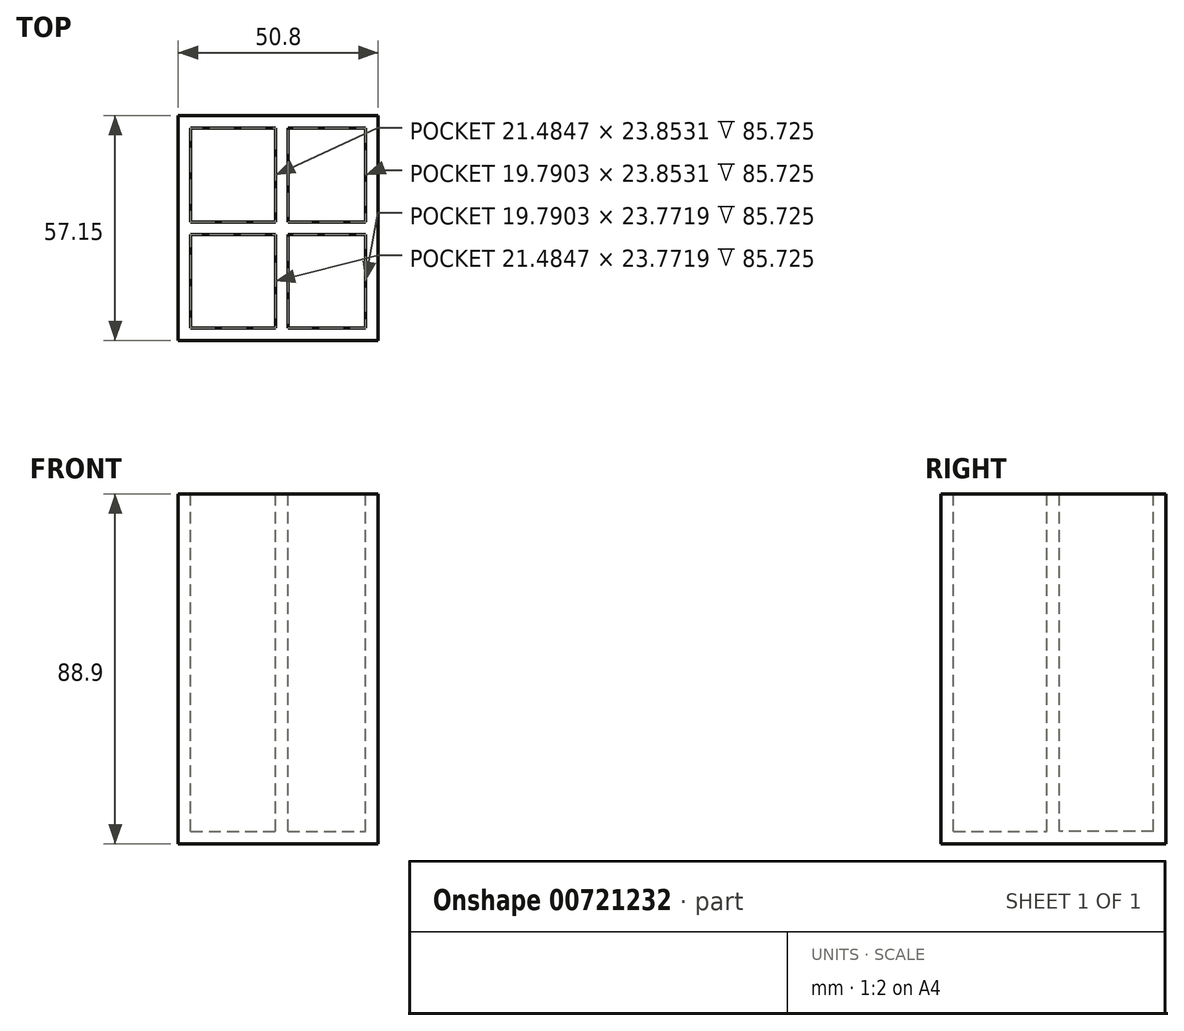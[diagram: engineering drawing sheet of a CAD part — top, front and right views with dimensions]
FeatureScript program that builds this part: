
annotation { "Feature Type Name" : "Feature", "Feature Type Description" : "" }
export const myFeature = defineFeature(function(context is Context, id is Id, definition is map)
    precondition{}
    {
        {
            var Q0;
            Q0=qCreatedBy(makeId("Top.planeOp"),FACE);
            var sketch = newSketch(context, id + "F0", { "sketchPlane" : qUnion([Q0])});
            skLineSegment(sketch, "E0.bottom", {"start": v(-26.25, 28.62) * mm, "end": v(24.55, 28.62) * mm});
            skLineSegment(sketch, "E0.top", {"start": v(-26.25, -28.53) * mm, "end": v(24.55, -28.53) * mm});
            skLineSegment(sketch, "E0.left", {"start": v(-26.25, 28.62) * mm, "end": v(-26.25, -28.53) * mm});
            skLineSegment(sketch, "E0.right", {"start": v(24.55, 28.62) * mm, "end": v(24.55, -28.53) * mm});
            skSolve(sketch);
        }
        {
            var Q0;
            Q0=makeQuery(id+"F0.imprint","IMPRINT",FACE,{"disambiguationData":[TD([[makeQuery(id+"F0.imprint","IMPRINT",EDGE,{"derivedFrom":sQuery(id+"F0.wireOp",EDGE,"E0.bottom")}),-1.0]])]});
            extrude(context, id + "F1", {"entities" : qUnion([Q0]), "depth" : 88.9 * mm, "offsetDistance" : 25.4 * mm});
        }
        {
            var Q0;
            Q0=makeQuery(id+"F1.opExtrude","CAP_FACE",FACE,{"disambiguationData":[OSD([sQuery(id+"F0.wireOp",EDGE,"E0.bottom"),sQuery(id+"F0.wireOp",EDGE,"E0.top"),sQuery(id+"F0.wireOp",EDGE,"E0.left"),sQuery(id+"F0.wireOp",EDGE,"E0.right")])],"isStart":false});
            var sketch = newSketch(context, id + "F2", { "sketchPlane" : qUnion([Q0])});
            skPoint(sketch, "E1.endSnap0", {"position": v(-0.85, -28.53) * mm});
            skLineSegment(sketch, "E2", {"start": v(-23.07, 1.59) * mm, "end": v(-1.59, 1.59) * mm});
            skLineSegment(sketch, "E3", {"start": v(-23.07, -1.59) * mm, "end": v(-1.59, -1.59) * mm});
            skLineSegment(sketch, "E4", {"start": v(-1.59, -25.36) * mm, "end": v(-1.59, -1.59) * mm});
            skLineSegment(sketch, "E5", {"start": v(1.59, -25.36) * mm, "end": v(1.59, -1.59) * mm});
            skLineSegment(sketch, "E6", {"start": v(-23.07, 25.44) * mm, "end": v(-23.07, 1.59) * mm});
            skLineSegment(sketch, "E7", {"start": v(-23.07, -25.36) * mm, "end": v(-1.59, -25.36) * mm});
            skLineSegment(sketch, "E8", {"start": v(21.38, 25.44) * mm, "end": v(21.38, 1.59) * mm});
            skLineSegment(sketch, "E9", {"start": v(-23.07, 25.44) * mm, "end": v(-1.59, 25.44) * mm});
            skLineSegment(sketch, "E10.trimOffspring", {"start": v(1.59, 1.59) * mm, "end": v(21.38, 1.59) * mm});
            skLineSegment(sketch, "E11.trimOffspring", {"start": v(1.59, 1.59) * mm, "end": v(1.59, 25.44) * mm});
            skLineSegment(sketch, "E12.trimOffspring", {"start": v(1.59, -1.59) * mm, "end": v(21.38, -1.59) * mm});
            skLineSegment(sketch, "E13.trimOffspring", {"start": v(-1.59, 1.59) * mm, "end": v(-1.59, 25.44) * mm});
            skLineSegment(sketch, "E14.trimOffspring", {"start": v(21.38, -1.59) * mm, "end": v(21.38, -25.36) * mm});
            skLineSegment(sketch, "E15.trimOffspring", {"start": v(1.59, -25.36) * mm, "end": v(21.38, -25.36) * mm});
            skLineSegment(sketch, "E16.trimOffspring", {"start": v(-23.07, -1.59) * mm, "end": v(-23.07, -25.36) * mm});
            skLineSegment(sketch, "E17.trimOffspring", {"start": v(1.59, 25.44) * mm, "end": v(21.38, 25.44) * mm});
            skSolve(sketch);
        }
        {
            var Q0;
            Q0=makeQuery(id+"F2.imprint","IMPRINT",FACE,{"disambiguationData":[TD([[makeQuery(id+"F2.imprint","IMPRINT",EDGE,{"derivedFrom":sQuery(id+"F2.wireOp",EDGE,"E2")}),1.0]])]});
            var Q1;
            Q1=makeQuery(id+"F2.imprint","IMPRINT",FACE,{"disambiguationData":[TD([[makeQuery(id+"F2.imprint","IMPRINT",EDGE,{"derivedFrom":sQuery(id+"F2.wireOp",EDGE,"E8")}),-1.0]])]});
            var Q2;
            Q2=makeQuery(id+"F2.imprint","IMPRINT",FACE,{"disambiguationData":[TD([[makeQuery(id+"F2.imprint","IMPRINT",EDGE,{"derivedFrom":sQuery(id+"F2.wireOp",EDGE,"E5")}),-1.0]])]});
            var Q3;
            Q3=makeQuery(id+"F2.imprint","IMPRINT",FACE,{"disambiguationData":[TD([[makeQuery(id+"F2.imprint","IMPRINT",EDGE,{"derivedFrom":sQuery(id+"F2.wireOp",EDGE,"E3")}),-1.0]])]});
            extrude(context, id + "F3", {"entities" : qUnion([Q0, Q1, Q2, Q3]), "operationType" : NewBodyOperationType.REMOVE, "oppositeDirection" : true, "depth" : 85.72 * mm, "offsetDistance" : 25.4 * mm});
        }
    });
